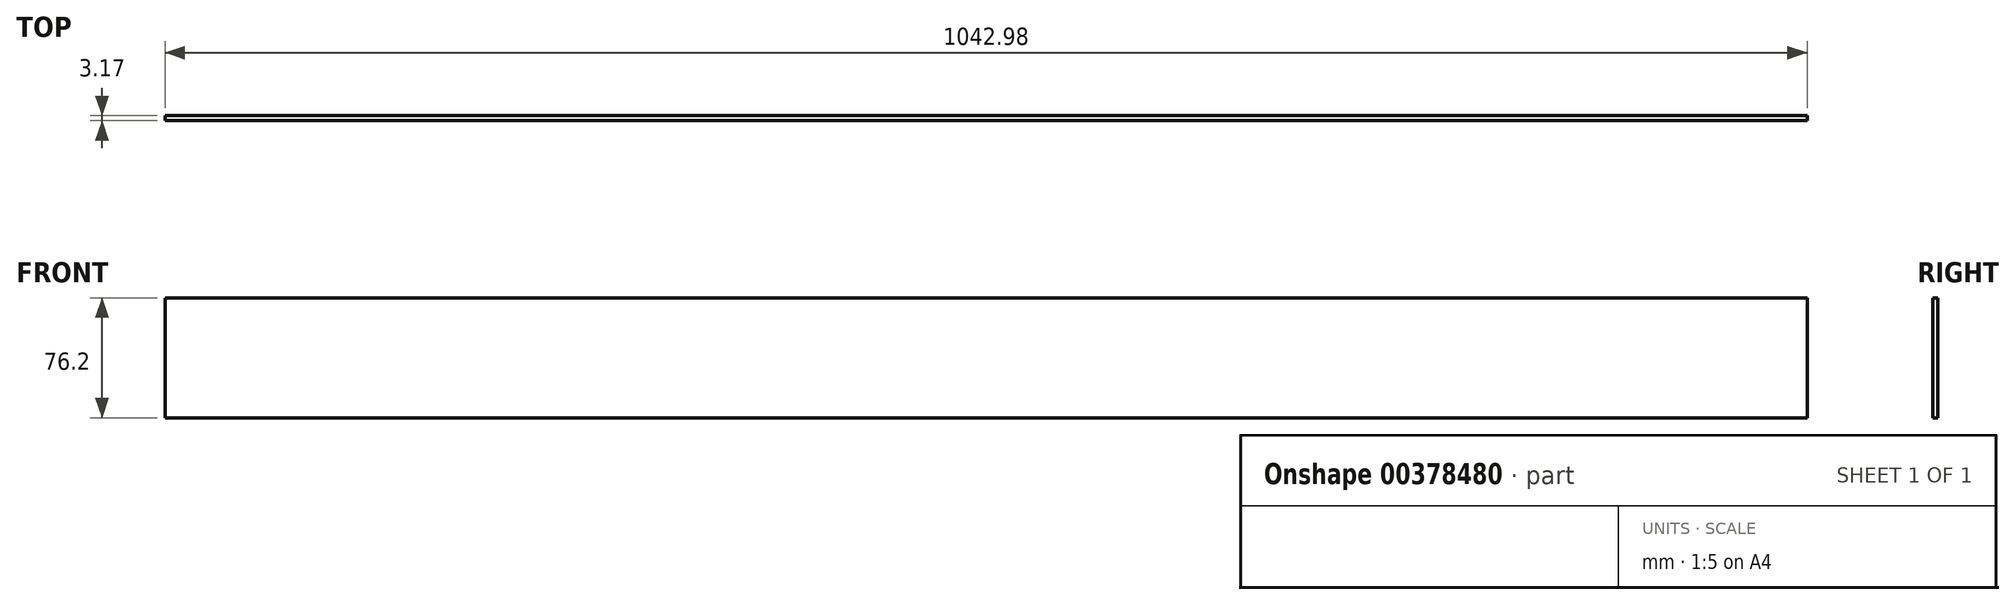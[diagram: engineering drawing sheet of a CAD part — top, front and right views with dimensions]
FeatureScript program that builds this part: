
annotation { "Feature Type Name" : "Feature", "Feature Type Description" : "" }
export const myFeature = defineFeature(function(context is Context, id is Id, definition is map)
    precondition{}
    {
        {
            var Q0;
            Q0=qCreatedBy(makeId("Front.planeOp"),FACE);
            var sketch = newSketch(context, id + "F0", { "sketchPlane" : qUnion([Q0])});
            skLineSegment(sketch, "E0.bottom", {"start": v(521.5, 38.1) * mm, "end": v(-521.5, 38.1) * mm});
            skLineSegment(sketch, "E0.top", {"start": v(521.5, -38.1) * mm, "end": v(-521.5, -38.1) * mm});
            skLineSegment(sketch, "E0.left", {"start": v(521.5, 38.1) * mm, "end": v(521.5, -38.1) * mm});
            skLineSegment(sketch, "E0.right", {"start": v(-521.5, 38.1) * mm, "end": v(-521.5, -38.1) * mm});
            skPoint(sketch, "E0.middle", {"position": v(0, 0) * mm});
            skSolve(sketch);
        }
        {
            var Q0;
            Q0 = qSketchRegion(id + "F0", true);
            extrude(context, id + "F1", {"entities" : qUnion([Q0]), "depth" : 3.17 * mm});
        }
    });
